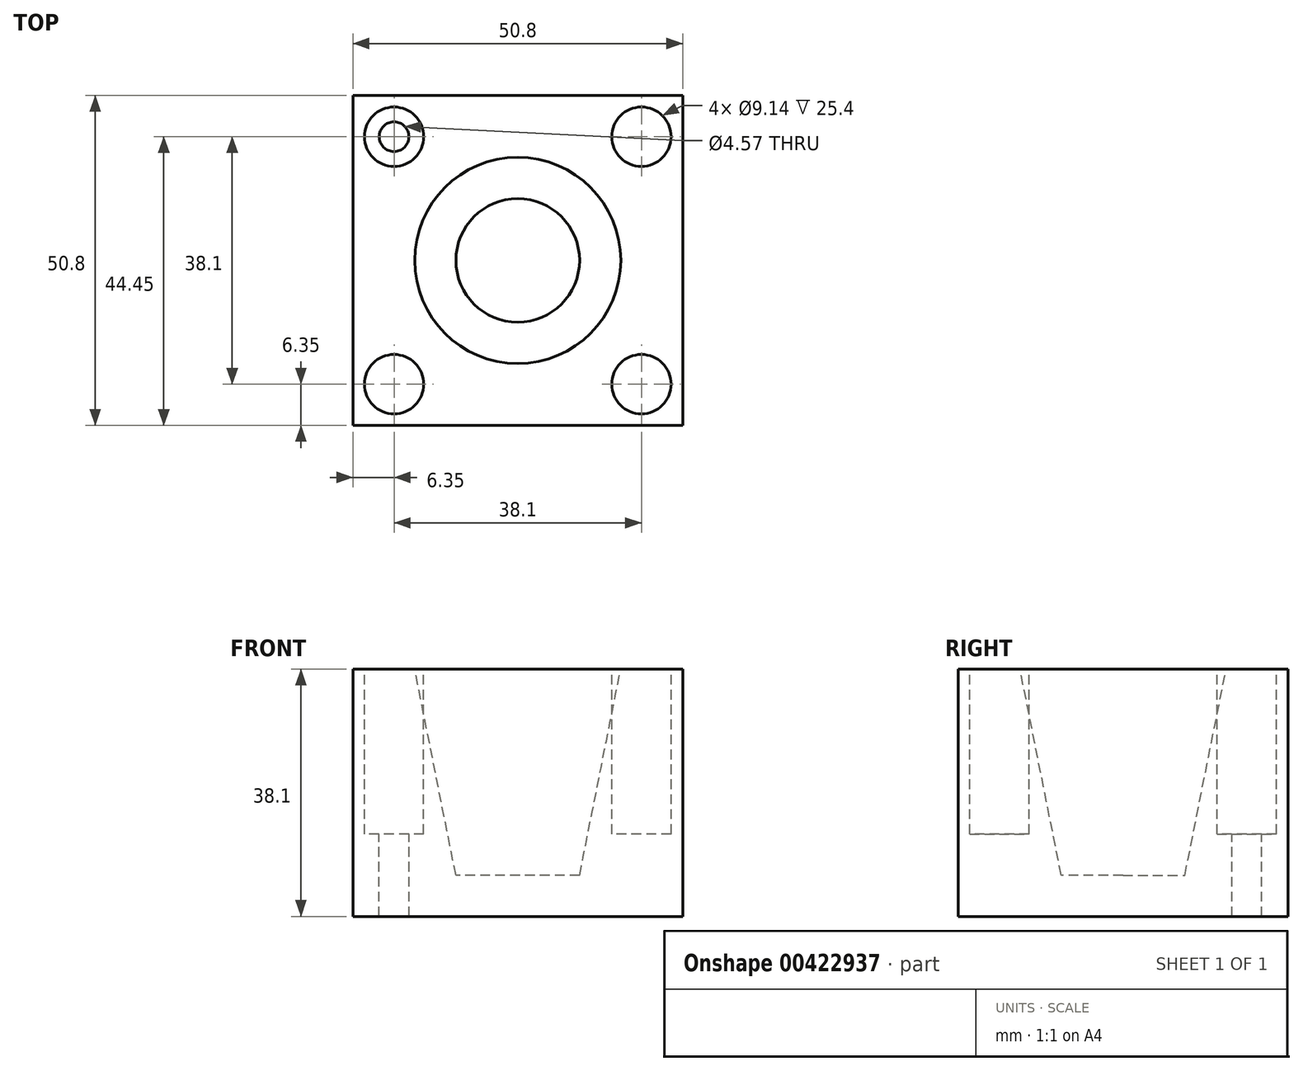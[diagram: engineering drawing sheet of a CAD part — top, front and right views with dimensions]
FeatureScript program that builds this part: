
annotation { "Feature Type Name" : "Feature", "Feature Type Description" : "" }
export const myFeature = defineFeature(function(context is Context, id is Id, definition is map)
    precondition{}
    {
        {
            var Q0;
            Q0=qCreatedBy(makeId("Top.planeOp"),FACE);
            var sketch = newSketch(context, id + "F0", { "sketchPlane" : qUnion([Q0])});
            skLineSegment(sketch, "E0.bottom", {"start": v(25.4, 25.4) * mm, "end": v(-25.4, 25.4) * mm});
            skLineSegment(sketch, "E0.top", {"start": v(25.4, -25.4) * mm, "end": v(-25.4, -25.4) * mm});
            skLineSegment(sketch, "E0.left", {"start": v(25.4, 25.4) * mm, "end": v(25.4, -25.4) * mm});
            skLineSegment(sketch, "E0.right", {"start": v(-25.4, 25.4) * mm, "end": v(-25.4, -25.4) * mm});
            skPoint(sketch, "E0.middle", {"position": v(0, 0) * mm});
            skSolve(sketch);
        }
        {
            var Q0;
            Q0=makeQuery(id+"F0.imprint","IMPRINT",FACE,{"disambiguationData":[TD([[makeQuery(id+"F0.imprint","IMPRINT",EDGE,{"derivedFrom":sQuery(id+"F0.wireOp",EDGE,"E0.bottom")}),1.0]])]});
            extrude(context, id + "F1", {"entities" : qUnion([Q0]), "depth" : 38.1 * mm});
        }
        {
            var Q0;
            Q0=makeQuery(id+"F1.opExtrude","CAP_FACE",FACE,{"disambiguationData":[OSD([sQuery(id+"F0.wireOp",EDGE,"E0.bottom"),sQuery(id+"F0.wireOp",EDGE,"E0.top"),sQuery(id+"F0.wireOp",EDGE,"E0.left"),sQuery(id+"F0.wireOp",EDGE,"E0.right")])],"isStart":false});
            var sketch = newSketch(context, id + "F2", { "sketchPlane" : qUnion([Q0])});
            skCircle(sketch, "E1", {"center": v(0, 0) * mm, "radius": 15.88 * mm});
            skSolve(sketch);
        }
        {
            var Q0;
            Q0=makeQuery(id+"F1.opExtrude","CAP_FACE",FACE,{"disambiguationData":[OSD([sQuery(id+"F0.wireOp",EDGE,"E0.bottom"),sQuery(id+"F0.wireOp",EDGE,"E0.top"),sQuery(id+"F0.wireOp",EDGE,"E0.left"),sQuery(id+"F0.wireOp",EDGE,"E0.right")])],"isStart":true});
            cPlane(context, id + "F3", {"entities" : qUnion([Q0]), "cplaneType" : CPlaneType.OFFSET, "offset" : 6.35 * mm, "oppositeDirection" : true, "width" : 152.4 * mm, "height" : 152.4 * mm});
        }
        {
            var Q0;
            Q0=qCreatedBy(id+"F3.planeOp",FACE);
            var sketch = newSketch(context, id + "F4", { "sketchPlane" : qUnion([Q0])});
            skCircle(sketch, "E2", {"center": v(0, 0) * mm, "radius": 9.53 * mm});
            skSolve(sketch);
        }
        {
            var Q1;
            Q1 = qSketchRegion(id + "F2", true);
            var Q2;
            Q2 = qSketchRegion(id + "F4", true);
            loft(context, id + "F5", {"operationType" : NewBodyOperationType.REMOVE, "sheetProfilesArray" : [{ "sheetProfileEntities" : qUnion([Q1]) }, { "sheetProfileEntities" : qUnion([Q2]) }]});
        }
        {
            var Q0;
            Q0=makeQuery(id+"F1.opExtrude","CAP_FACE",FACE,{"disambiguationData":[OSD([sQuery(id+"F0.wireOp",EDGE,"E0.bottom"),sQuery(id+"F0.wireOp",EDGE,"E0.top"),sQuery(id+"F0.wireOp",EDGE,"E0.left"),sQuery(id+"F0.wireOp",EDGE,"E0.right")])],"isStart":false});
            var sketch = newSketch(context, id + "F6", { "sketchPlane" : qUnion([Q0])});
            skCircle(sketch, "E3", {"center": v(19.05, -19.05) * mm, "radius": 4.57 * mm});
            skCircle(sketch, "E4.1.0", {"center": v(19.05, 19.05) * mm, "radius": 4.57 * mm});
            skCircle(sketch, "E4.2.0", {"center": v(-19.05, 19.05) * mm, "radius": 4.57 * mm});
            skCircle(sketch, "E4.3.0", {"center": v(-19.05, -19.05) * mm, "radius": 4.57 * mm});
            skPoint(sketch, "E4.center", {"position": v(0, 0) * mm});
            skSolve(sketch);
        }
        {
            var Q0;
            Q0 = qSketchRegion(id + "F6", true);
            extrude(context, id + "F7", {"entities" : qUnion([Q0]), "operationType" : NewBodyOperationType.REMOVE, "oppositeDirection" : true, "depth" : 25.4 * mm});
        }
        {
            var Q0;
            Q0=makeQuery(id+"F7.boolean.opBoolean","COPY",FACE,{"derivedFrom":makeQuery(id+"F7.opExtrude","CAP_FACE",FACE,{"disambiguationData":[OSD([sQuery(id+"F6.wireOp",EDGE,"E4.1.0")])],"isStart":false})});
            cPlane(context, id + "F8", {"entities" : qUnion([Q0]), "cplaneType" : CPlaneType.OFFSET, "offset" : 0 * mm, "width" : 152.4 * mm, "height" : 152.4 * mm});
        }
        {
            var Q0;
            Q0=qCreatedBy(id+"F8.planeOp",FACE);
            var sketch = newSketch(context, id + "F9", { "sketchPlane" : qUnion([Q0])});
            skCircle(sketch, "E5", {"center": v(-19.05, 19.05) * mm, "radius": 2.29 * mm});
            skSolve(sketch);
        }
        {
            var Q0;
            Q0 = qSketchRegion(id + "F9", true);
            extrude(context, id + "F10", {"entities" : qUnion([Q0]), "operationType" : NewBodyOperationType.REMOVE, "endBound" : BoundingType.THROUGH_ALL, "oppositeDirection" : true, "depth" : 25.4 * mm});
        }
        {
            var Q0;
            Q0=qCreatedBy(makeId("Front.planeOp"),FACE);
            var sketch = newSketch(context, id + "F11", { "sketchPlane" : qUnion([Q0])});
            skLineSegment(sketch, "E6", {"start": v(0, 0) * mm, "end": v(0, 58.56) * mm, "construction": true});
            skSolve(sketch);
        }
    });
